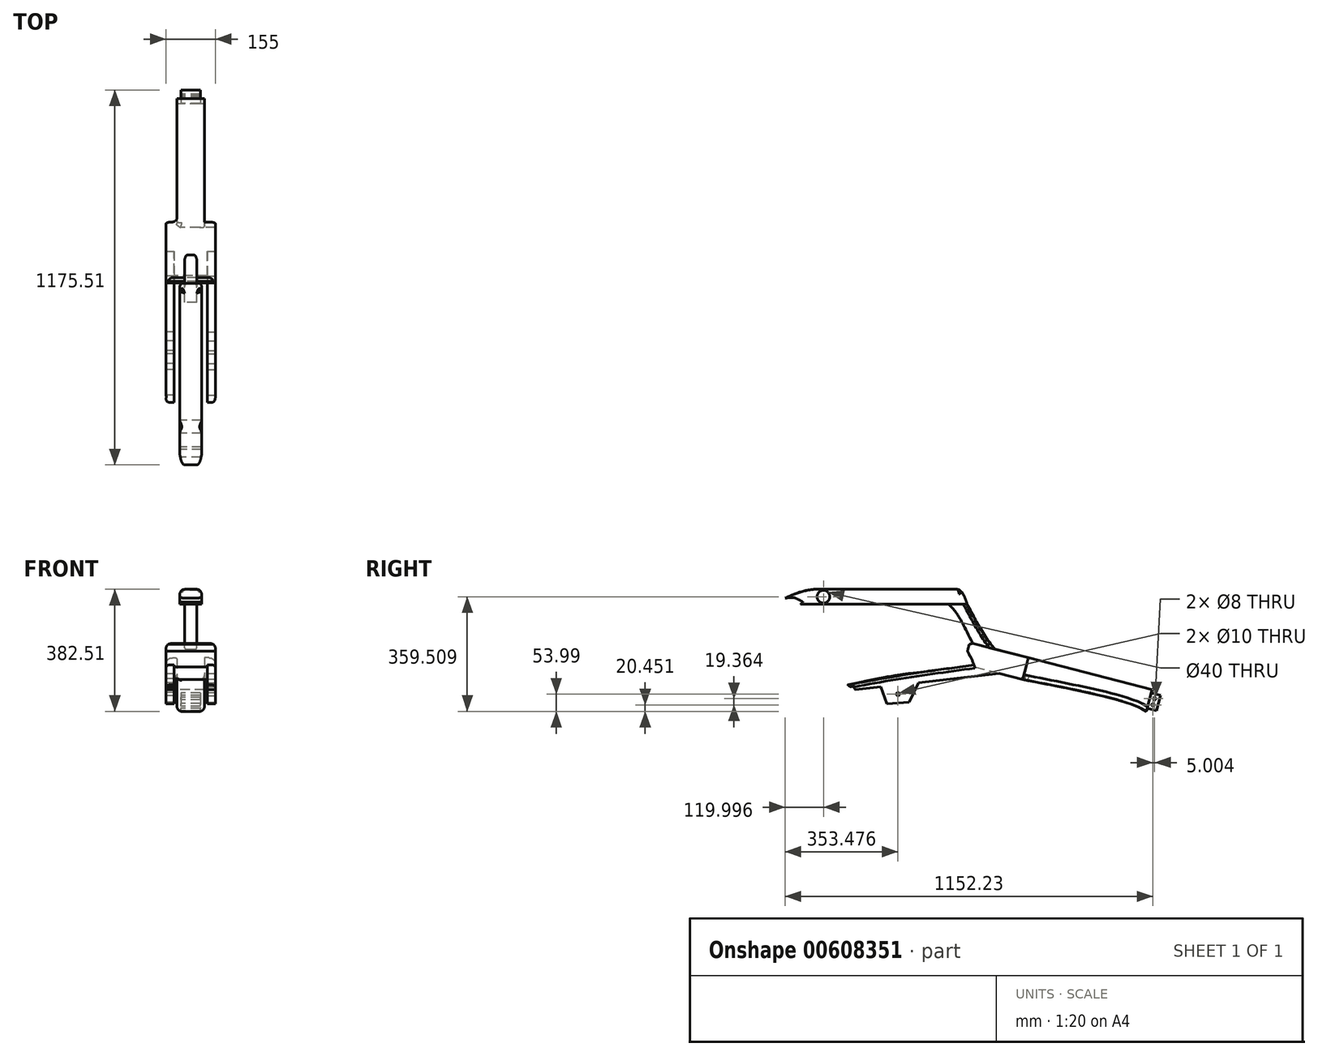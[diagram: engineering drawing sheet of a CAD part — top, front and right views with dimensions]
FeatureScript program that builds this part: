
annotation { "Feature Type Name" : "Feature", "Feature Type Description" : "" }
export const myFeature = defineFeature(function(context is Context, id is Id, definition is map)
    precondition{}
    {
        {
            var Q0;
            Q0=qCreatedBy(makeId("Right.planeOp"),FACE);
            var sketch = newSketch(context, id + "F0", { "sketchPlane" : qUnion([Q0])});
            skLineSegment(sketch, "E0", {"start": v(-839.21, 0) * mm, "end": v(-890, 0) * mm, "construction": true});
            skLineSegment(sketch, "E1", {"start": v(-890, 0) * mm, "end": v(-890, 230) * mm, "construction": true});
            skLineSegment(sketch, "E2", {"start": v(-890, 230) * mm, "end": v(0, 0) * mm, "construction": true});
            skCircle(sketch, "E3", {"center": v(-636.21, 0) * mm, "radius": 203 * mm});
            skCircle(sketch, "E4", {"center": v(513.79, 0) * mm, "radius": 203 * mm});
            skLineSegment(sketch, "E5.bottom", {"start": v(-636.21, 0) * mm, "end": v(513.79, 0) * mm, "construction": true});
            skLineSegment(sketch, "E6", {"start": v(-839.21, 0) * mm, "end": v(-636.21, 0) * mm, "construction": true});
            skCircle(sketch, "E7.0", {"center": v(-636.21, 0) * mm, "radius": 248 * mm});
            skCircle(sketch, "E8.0", {"center": v(513.79, 0) * mm, "radius": 248 * mm});
            skLineSegment(sketch, "E9", {"start": v(0, 0) * mm, "end": v(19.52, 75.52) * mm, "construction": true});
            skLineSegment(sketch, "E10", {"start": v(19.52, 75.52) * mm, "end": v(-870.48, 305.52) * mm, "construction": true});
            skLineSegment(sketch, "E11", {"start": v(-870.48, 305.52) * mm, "end": v(-890, 230) * mm, "construction": true});
            skCircle(sketch, "E12", {"center": v(-870.48, 305.52) * mm, "radius": 22.5 * mm});
            skCircle(sketch, "E13", {"center": v(-870.48, 305.52) * mm, "radius": 21 * mm});
            skCircle(sketch, "E14", {"center": v(-870.48, 305.52) * mm, "radius": 110 * mm});
            skLineSegment(sketch, "E15", {"start": v(19.52, 75.52) * mm, "end": v(573.04, 539.98) * mm, "construction": true});
            skLineSegment(sketch, "E16", {"start": v(-86.27, 75.52) * mm, "end": v(113.73, 75.52) * mm, "construction": true});
            skLineSegment(sketch, "E17", {"start": v(-636.21, 0) * mm, "end": v(-636.21, -248) * mm, "construction": true});
            skLineSegment(sketch, "E18", {"start": v(-636.21, -248) * mm, "end": v(513.79, -248) * mm, "construction": true});
            skLineSegment(sketch, "E19", {"start": v(513.79, -248) * mm, "end": v(513.79, 0) * mm, "construction": true});
            skSolve(sketch);
        }
        {
            var Q0;
            Q0=qCreatedBy(makeId("Right.planeOp"),FACE);
            cPlane(context, id + "F1", {"entities" : qUnion([Q0]), "cplaneType" : CPlaneType.OFFSET, "offset" : 65 * mm, "oppositeDirection" : true, "width" : 150 * mm, "height" : 150 * mm});
        }
        {
            var Q0;
            Q0=qCreatedBy(makeId("Right.planeOp"),FACE);
            cPlane(context, id + "F2", {"entities" : qUnion([Q0]), "cplaneType" : CPlaneType.OFFSET, "offset" : 65 * mm, "width" : 150 * mm, "height" : 150 * mm});
        }
        {
            var Q0;
            Q0=qCreatedBy(makeId("Right.planeOp"),FACE);
            var sketch = newSketch(context, id + "F3", { "sketchPlane" : qUnion([Q0])});
            skLineSegment(sketch, "E20", {"start": v(-228.79, 113.87) * mm, "end": v(158.49, 13.78) * mm});
            skLineSegment(sketch, "E21.bottom", {"start": v(-990.48, 328.52) * mm, "end": v(-420.48, 328.52) * mm, "construction": true});
            skLineSegment(sketch, "E21.top", {"start": v(-990.48, 282.52) * mm, "end": v(-420.48, 282.52) * mm, "construction": true});
            skLineSegment(sketch, "E21.left", {"start": v(-990.48, 328.52) * mm, "end": v(-990.48, 282.52) * mm, "construction": true});
            skLineSegment(sketch, "E21.right", {"start": v(-420.48, 328.52) * mm, "end": v(-420.48, 282.52) * mm, "construction": true});
            skLineSegment(sketch, "E22", {"start": v(-228.79, 113.87) * mm, "end": v(-403.06, 158.9) * mm});
            skLineSegment(sketch, "E23", {"start": v(-412.74, 161.4) * mm, "end": v(-430.26, 93.63) * mm, "construction": true});
            skLineSegment(sketch, "E24", {"start": v(-430.26, 93.63) * mm, "end": v(-246.3, 46.1) * mm, "construction": true});
            skLineSegment(sketch, "E25", {"start": v(158.49, 13.78) * mm, "end": v(140.98, -54) * mm});
            skLineSegment(sketch, "E26", {"start": v(-228.79, 113.87) * mm, "end": v(-246.3, 46.1) * mm});
            skLineSegment(sketch, "E27", {"start": v(-990.48, 305.52) * mm, "end": v(-420.48, 305.52) * mm, "construction": true});
            skLineSegment(sketch, "E28", {"start": v(-420.48, 282.52) * mm, "end": v(-331.58, 140.43) * mm, "construction": true});
            skLineSegment(sketch, "E29", {"start": v(-480.4, 282.52) * mm, "end": v(-403.06, 158.9) * mm, "construction": true});
            skCircle(sketch, "E30", {"center": v(-870.48, 305.52) * mm, "radius": 20 * mm});
            skFitSpline(sketch, "E31", {"points": [v(-446.93, 328.52) * mm, v(-420.48, 282.52) * mm], "startDerivative": vector(40.95, -24.88) * mm, "endDerivative": vector(18.36, -59.68) * mm});
            skLineSegment(sketch, "E32", {"start": v(-480.4, 282.52) * mm, "end": v(-420.48, 282.52) * mm});
            skFitSpline(sketch, "E33", {"points": [v(-480.4, 282.52) * mm, v(-403.06, 158.9) * mm], "startDerivative": vector(83.68, -66.51) * mm, "endDerivative": vector(113.52, -228.08) * mm});
            skFitSpline(sketch, "E34", {"points": [v(-420.48, 282.52) * mm, v(-331.58, 140.43) * mm], "startDerivative": vector(46.18, -95.07) * mm, "endDerivative": vector(81.7, -70.02) * mm});
            skLineSegment(sketch, "E35", {"start": v(-396.57, 84.92) * mm, "end": v(-246.3, 46.1) * mm});
            skFitSpline(sketch, "E36", {"points": [v(-419.66, 134.65) * mm, v(-396.57, 84.92) * mm], "startDerivative": vector(31.98, -52.88) * mm, "endDerivative": vector(7.26, -32.36) * mm});
            skFitSpline(sketch, "E37", {"points": [v(-403.06, 158.9) * mm, v(-414.1, 156.15) * mm], "startDerivative": vector(-13.37, -1.9) * mm, "endDerivative": vector(-11.19, -2.08) * mm});
            skFitSpline(sketch, "E38", {"points": [v(-414.1, 156.15) * mm, v(-419.66, 134.65) * mm], "startDerivative": vector(-4.9, -18.97) * mm, "endDerivative": vector(0.06, 8.38) * mm});
            skLineSegment(sketch, "E39", {"start": v(-430.26, 93.63) * mm, "end": v(140.98, -54) * mm, "construction": true});
            skFitSpline(sketch, "E40", {"points": [v(-246.3, 46.1) * mm, v(140.98, -54) * mm], "startDerivative": vector(593.3, -116.1) * mm, "endDerivative": vector(155.05, -104.97) * mm});
            skCircle(sketch, "E41", {"center": v(166.76, -14.17) * mm, "radius": 4 * mm});
            skCircle(sketch, "E42", {"center": v(161.75, -33.54) * mm, "radius": 4 * mm});
            skLineSegment(sketch, "E43", {"start": v(-900.48, 328.52) * mm, "end": v(-870.48, 305.52) * mm, "construction": true});
            skFitSpline(sketch, "E44", {"points": [v(-900.48, 328.52) * mm, v(-990.48, 301.22) * mm], "startDerivative": vector(-118.47, -11.59) * mm, "endDerivative": vector(-75.39, -34.72) * mm});
            skLineSegment(sketch, "E45", {"start": v(-900.48, 328.52) * mm, "end": v(-446.93, 328.52) * mm});
            skLineSegment(sketch, "E46", {"start": v(-420.48, 282.52) * mm, "end": v(-941.99, 282.52) * mm});
            skFitSpline(sketch, "E47", {"points": [v(-990.48, 301.22) * mm, v(-966.17, 303.05) * mm], "startDerivative": vector(15.61, 2.31) * mm, "endDerivative": vector(15.61, 2.31) * mm});
            skFitSpline(sketch, "E48", {"points": [v(-966.17, 303.05) * mm, v(-934.37, 289.04) * mm], "startDerivative": vector(29.52, -2.6) * mm, "endDerivative": vector(28.82, -13.66) * mm});
            skFitSpline(sketch, "E49", {"points": [v(-934.37, 289.04) * mm, v(-941.99, 282.52) * mm], "startDerivative": vector(-7.1, -7.67) * mm, "endDerivative": vector(-7.31, -5.1) * mm});
            skLineSegment(sketch, "E50", {"start": v(-480.4, 282.52) * mm, "end": v(-361.43, 356.97) * mm, "construction": true});
            skLineSegment(sketch, "E51", {"start": v(-331.58, 140.43) * mm, "end": v(-237.61, 199.22) * mm, "construction": true});
            skLineSegment(sketch, "E52", {"start": v(155.99, 4.1) * mm, "end": v(185.03, -3.4) * mm});
            skLineSegment(sketch, "E53", {"start": v(185.03, -3.4) * mm, "end": v(172.52, -51.81) * mm});
            skLineSegment(sketch, "E54", {"start": v(172.52, -51.81) * mm, "end": v(143.48, -44.3) * mm});
            skLineSegment(sketch, "E55", {"start": v(170.51, 0.35) * mm, "end": v(158, -48.06) * mm, "construction": true});
            skSolve(sketch);
        }
        {
            var Q0;
            Q0=makeQuery(id+"F3.imprint","IMPRINT",FACE,{"disambiguationData":[TD([[makeQuery(id+"F3.imprint","IMPRINT",EDGE,{"derivedFrom":sQuery(id+"F3.wireOp",EDGE,"E30")}),-1.0]])]});
            extrude(context, id + "F4", {"entities" : qUnion([Q0]), "endBound" : BoundingType.SYMMETRIC, "depth" : 68 * mm, "offsetDistance" : 25 * mm});
        }
        {
            var Q0;
            {var subQ0=sQuery(id+"F3.wireOp",EDGE,"E33");Q0=makeQuery(id+"F3.imprint","IMPRINT",FACE,{"disambiguationData":[TD([[makeQuery(id+"F3.imprint","IMPRINT",EDGE,{"derivedFrom":subQ0}),1.0]])]});}
            extrude(context, id + "F5", {"entities" : qUnion([Q0]), "operationType" : NewBodyOperationType.ADD, "endBound" : BoundingType.SYMMETRIC, "depth" : 38.1 * mm, "offsetDistance" : 25 * mm});
        }
        {
            var Q0;
            {var subQ3=sQuery(id+"F3.wireOp",EDGE,"E26");Q0=makeQuery(id+"F3.imprint","IMPRINT",FACE,{"disambiguationData":[TD([[makeQuery(id+"F3.imprint","IMPRINT",EDGE,{"derivedFrom":subQ3}),-1.0]])]});}
            extrude(context, id + "F6", {"entities" : qUnion([Q0]), "operationType" : NewBodyOperationType.ADD, "endBound" : BoundingType.SYMMETRIC, "depth" : 155 * mm, "offsetDistance" : 25 * mm});
        }
        {
            var Q0;
            Q0=makeQuery(id+"F6.opExtrude","CAP_FACE",FACE,{"disambiguationData":[OSD([sQuery(id+"F3.wireOp",EDGE,"E20"),sQuery(id+"F3.wireOp",EDGE,"E22"),sQuery(id+"F3.wireOp",EDGE,"E23"),sQuery(id+"F3.wireOp",EDGE,"E24"),sQuery(id+"F3.wireOp",EDGE,"fels3fzP-0Cul-zycu-sXH3-jASdoxwQIRJ3"),sQuery(id+"F3.wireOp",EDGE,"7BiVgZWP-wgUI-RrVQ-dbGp-AfqpS34TpyPq")])],"isStart":false});
            var sketch = newSketch(context, id + "F7", { "sketchPlane" : qUnion([Q0])});
            skLineSegment(sketch, "E56", {"start": v(-304.09, 102.34) * mm, "end": v(-257.8, 93.53) * mm, "construction": true});
            skLineSegment(sketch, "E57", {"start": v(-257.8, 93.53) * mm, "end": v(-255.41, 72.67) * mm, "construction": true});
            skLineSegment(sketch, "E58", {"start": v(-255.41, 72.67) * mm, "end": v(-791.93, 11.44) * mm, "construction": true});
            skLineSegment(sketch, "E59", {"start": v(-791.93, 11.44) * mm, "end": v(-795.9, 46.22) * mm, "construction": true});
            skLineSegment(sketch, "E60", {"start": v(-795.9, 46.22) * mm, "end": v(-304.09, 102.34) * mm, "construction": true});
            skLineSegment(sketch, "E61", {"start": v(-573.32, 36.39) * mm, "end": v(-601.7, -25.77) * mm});
            skLineSegment(sketch, "E62", {"start": v(-601.7, -25.77) * mm, "end": v(-672.4, -29.77) * mm});
            skLineSegment(sketch, "E63", {"start": v(-672.4, -29.77) * mm, "end": v(-691.03, 22.96) * mm});
            skCircle(sketch, "E64", {"center": v(-637, 0) * mm, "radius": 5 * mm});
            skPoint(sketch, "E65", {"position": v(-320.43, 65.25) * mm});
            skLineSegment(sketch, "E66", {"start": v(-255.41, 72.67) * mm, "end": v(-771.24, 13.8) * mm});
            skFitSpline(sketch, "E67", {"points": [v(-771.24, 13.8) * mm, v(-793.91, 28.83) * mm], "startDerivative": vector(-11.51, 40.5) * mm, "endDerivative": vector(-30.67, 16.33) * mm});
            skLineSegment(sketch, "E68", {"start": v(-304.09, 102.34) * mm, "end": v(-398.53, 91.56) * mm});
            skLineSegment(sketch, "E69", {"start": v(-304.09, 102.34) * mm, "end": v(-257.8, 93.53) * mm});
            skLineSegment(sketch, "E70", {"start": v(-255.41, 72.67) * mm, "end": v(-257.8, 93.53) * mm});
            skFitSpline(sketch, "E71", {"points": [v(-398.53, 91.56) * mm, v(-793.91, 28.83) * mm], "startDerivative": vector(-396.31, -54.62) * mm, "endDerivative": vector(-425.7, -85.53) * mm});
            skSolve(sketch);
        }
        {
            var Q0;
            Q0=makeQuery(id+"F3.imprint","IMPRINT",FACE,{"disambiguationData":[TD([[makeQuery(id+"F3.imprint","IMPRINT",EDGE,{"derivedFrom":sQuery(id+"F3.wireOp",EDGE,"E20")}),-1.0]])]});
            extrude(context, id + "F8", {"entities" : qUnion([Q0]), "operationType" : NewBodyOperationType.ADD, "endBound" : BoundingType.SYMMETRIC, "depth" : 86 * mm, "offsetDistance" : 25 * mm});
        }
        {
            var Q0;
            Q0=makeQuery(id+"F6.opExtrude","CAP_FACE",FACE,{"disambiguationData":[OSD([sQuery(id+"F3.wireOp",EDGE,"E22"),sQuery(id+"F3.wireOp",EDGE,"E23"),sQuery(id+"F3.wireOp",EDGE,"E24"),sQuery(id+"F3.wireOp",EDGE,"E26")])],"isStart":true});
            var sketch = newSketch(context, id + "F9", { "sketchPlane" : qUnion([Q0])});
            skLineSegment(sketch, "E72.0.0", {"start": v(573.32, 36.39) * mm, "end": v(320.43, 65.25) * mm});
            skLineSegment(sketch, "E72.0.1", {"start": v(320.43, 65.25) * mm, "end": v(396.57, 84.92) * mm});
            skFitSpline(sketch, "E72.0.2", {"points": [v(396.57, 84.92) * mm, v(398.98, 95.71) * mm, v(409, 117.02) * mm, v(419.66, 134.65) * mm]});
            skFitSpline(sketch, "E72.0.3", {"points": [v(398.53, 91.56) * mm, v(530.63, 73.36) * mm, v(652.01, 57.34) * mm, v(793.91, 28.83) * mm]});
            skFitSpline(sketch, "E72.0.4", {"points": [v(793.91, 28.83) * mm, v(783.7, 23.39) * mm, v(775.08, 27.3) * mm, v(771.24, 13.8) * mm]});
            skLineSegment(sketch, "E72.0.5", {"start": v(771.24, 13.8) * mm, "end": v(691.03, 22.96) * mm});
            skLineSegment(sketch, "E72.0.6", {"start": v(691.03, 22.96) * mm, "end": v(573.32, 36.39) * mm});
            skLineSegment(sketch, "E73.0.0", {"start": v(601.7, -25.77) * mm, "end": v(573.32, 36.39) * mm});
            skLineSegment(sketch, "E73.0.1", {"start": v(573.32, 36.39) * mm, "end": v(691.03, 22.96) * mm});
            skLineSegment(sketch, "E73.0.2", {"start": v(691.03, 22.96) * mm, "end": v(672.4, -29.77) * mm});
            skLineSegment(sketch, "E73.0.3", {"start": v(672.4, -29.77) * mm, "end": v(601.7, -25.77) * mm});
            skCircle(sketch, "E74.0", {"center": v(637, 0) * mm, "radius": 5 * mm});
            skLineSegment(sketch, "E75.0.0", {"start": v(257.8, 93.53) * mm, "end": v(304.09, 102.34) * mm});
            skLineSegment(sketch, "E75.0.1", {"start": v(304.09, 102.34) * mm, "end": v(398.53, 91.56) * mm});
            skFitSpline(sketch, "E75.0.2", {"points": [v(419.66, 134.65) * mm, v(409, 117.02) * mm, v(398.98, 95.71) * mm, v(396.57, 84.92) * mm]});
            skLineSegment(sketch, "E75.0.3", {"start": v(396.57, 84.92) * mm, "end": v(320.43, 65.25) * mm});
            skLineSegment(sketch, "E75.0.4", {"start": v(320.43, 65.25) * mm, "end": v(255.41, 72.67) * mm});
            skLineSegment(sketch, "E75.0.5", {"start": v(255.41, 72.67) * mm, "end": v(257.8, 93.53) * mm});
            skSolve(sketch);
        }
        {
            var Q0;
            Q0=makeQuery(id+"F3.imprint","IMPRINT",FACE,{"disambiguationData":[TD([[makeQuery(id+"F3.imprint","IMPRINT",EDGE,{"derivedFrom":sQuery(id+"F3.wireOp",EDGE,"E41")}),-1.0]])]});
            extrude(context, id + "F10", {"entities" : qUnion([Q0]), "operationType" : NewBodyOperationType.ADD, "endBound" : BoundingType.SYMMETRIC, "depth" : 60 * mm, "offsetDistance" : 25 * mm});
        }
        {
            var Q0;
            {var subQ0=sQuery(id+"F7.wireOp",EDGE,"E67");Q0=makeQuery(id+"F7.imprint","IMPRINT",FACE,{"disambiguationData":[TD([[makeQuery(id+"F7.imprint","IMPRINT",EDGE,{"derivedFrom":subQ0}),-1.0]])]});}
            var Q1;
            {var subQ1=sQuery(id+"F7.wireOp",EDGE,"E61");Q1=makeQuery(id+"F7.imprint","IMPRINT",FACE,{"disambiguationData":[TD([[makeQuery(id+"F7.imprint","IMPRINT",EDGE,{"derivedFrom":subQ1}),-1.0]])]});}
            var Q2;
            {var subQ1=sQuery(id+"F7.wireOp",EDGE,"E68");Q2=makeQuery(id+"F7.imprint","IMPRINT",FACE,{"disambiguationData":[TD([[makeQuery(id+"F7.imprint","IMPRINT",EDGE,{"derivedFrom":subQ1}),1.0]])]});}
            extrude(context, id + "F11", {"entities" : qUnion([Q0, Q1, Q2]), "operationType" : NewBodyOperationType.ADD, "oppositeDirection" : true, "depth" : 25.4 * mm, "offsetDistance" : 25 * mm});
        }
        {
            var Q0;
            Q0=makeQuery(id+"F8.opExtrude","CAP_EDGE",EDGE,{"disambiguationData":[OSD([sQuery(id+"F3.wireOp",EDGE,"E26")])],"isStart":true});
            var Q1;
            Q1=makeQuery(id+"F8.opExtrude","CAP_EDGE",EDGE,{"disambiguationData":[OSD([sQuery(id+"F3.wireOp",EDGE,"E26")])],"isStart":false});
            var Q2;
            Q2=makeQuery(id+"F4.opExtrude","CAP_EDGE",EDGE,{"disambiguationData":[OSD([sQuery(id+"F3.wireOp",EDGE,"E45")])],"isStart":false});
            var Q3;
            Q3=makeQuery(id+"F4.opExtrude","CAP_EDGE",EDGE,{"disambiguationData":[OSD([sQuery(id+"F3.wireOp",EDGE,"E45")])],"isStart":true});
            var Q4;
            Q4=makeQuery(id+"F4.opExtrude","CAP_EDGE",EDGE,{"disambiguationData":[OSD([sQuery(id+"F3.wireOp",EDGE,"E44")])],"isStart":false});
            var Q5;
            Q5=makeQuery(id+"F4.opExtrude","CAP_EDGE",EDGE,{"disambiguationData":[OSD([sQuery(id+"F3.wireOp",EDGE,"E44")])],"isStart":true});
            var Q6;
            Q6=makeQuery(id+"F4.opExtrude","SWEPT_EDGE",EDGE,{"disambiguationData":[OSD([sQuery(id+"F3.wireOp",EDGE,"E31"),sQuery(id+"F3.wireOp",EDGE,"E45")])]});
            var Q7;
            Q7=makeQuery(id+"F4.opExtrude","SWEPT_EDGE",EDGE,{"disambiguationData":[OSD([sQuery(id+"F3.wireOp",EDGE,"E44"),sQuery(id+"F3.wireOp",EDGE,"E45")])]});
            fillet(context, id + "F12", {"entities" : qUnion([Q0, Q1, Q2, Q3, Q4, Q5, Q6, Q7]), "radius" : 15 * mm, "tangentPropagation" : true, "allowEdgeOverflow" : false});
        }
        {
            var Q0;
            Q0=makeQuery(id+"F5.opExtrude","CAP_EDGE",EDGE,{"disambiguationData":[OSD([sQuery(id+"F3.wireOp",EDGE,"E34")])],"isStart":false});
            var Q1;
            Q1=makeQuery(id+"F5.opExtrude","CAP_EDGE",EDGE,{"disambiguationData":[OSD([sQuery(id+"F3.wireOp",EDGE,"E34")])],"isStart":true});
            var Q2;
            Q2=makeQuery(id+"F11.opExtrude","CAP_EDGE",EDGE,{"disambiguationData":[OSD([sQuery(id+"F7.wireOp",EDGE,"2d2ba40c-a02e-4269-819a-9c400366be13")])],"isStart":true});
            var Q3;
            Q3=makeQuery(id+"FFKQbZDGYRM2YjH_1.opExtrude","CAP_EDGE",EDGE,{"disambiguationData":[OSD([sQuery(id+"F9.wireOp",EDGE,"418496da-3a12-4d16-a20d-26360628b4ec.2")])],"isStart":true});
            var Q4;
            Q4=makeQuery(id+"F4.opExtrude","CAP_EDGE",EDGE,{"disambiguationData":[OSD([sQuery(id+"F3.wireOp",EDGE,"E31")])],"isStart":false});
            var Q5;
            Q5=makeQuery(id+"F4.opExtrude","CAP_EDGE",EDGE,{"disambiguationData":[OSD([sQuery(id+"F3.wireOp",EDGE,"E31")])],"isStart":true});
            fillet(context, id + "F13", {"entities" : qUnion([Q0, Q1, Q2, Q3, Q4, Q5]), "radius" : 10 * mm, "tangentPropagation" : true, "allowEdgeOverflow" : false});
        }
        {
            var Q0;
            Q0=makeQuery(id+"F4.opExtrude","CAP_EDGE",EDGE,{"disambiguationData":[OSD([sQuery(id+"F3.wireOp",EDGE,"81e0ebba-2043-46d8-adfa-aa85b01486f9")])],"isStart":true});
            var Q1;
            Q1=makeQuery(id+"F4.opExtrude","CAP_EDGE",EDGE,{"disambiguationData":[OSD([sQuery(id+"F3.wireOp",EDGE,"81e0ebba-2043-46d8-adfa-aa85b01486f9")])],"isStart":false});
            var Q2;
            Q2=makeQuery(id+"F6.opExtrude","CAP_EDGE",EDGE,{"disambiguationData":[OSD([sQuery(id+"F3.wireOp",EDGE,"E22")])],"isStart":false});
            var Q3;
            Q3=makeQuery(id+"F6.opExtrude","CAP_EDGE",EDGE,{"disambiguationData":[OSD([sQuery(id+"F3.wireOp",EDGE,"E22")])],"isStart":true});
            fillet(context, id + "F14", {"entities" : qUnion([Q0, Q1, Q2, Q3]), "radius" : 20 * mm, "tangentPropagation" : true, "allowEdgeOverflow" : false});
        }
        {
            var Q0;
            Q0=makeQuery(id+"F8.opExtrude","CAP_EDGE",EDGE,{"disambiguationData":[OSD([sQuery(id+"F3.wireOp",EDGE,"E40")])],"isStart":false});
            var Q1;
            Q1=makeQuery(id+"F8.opExtrude","CAP_EDGE",EDGE,{"disambiguationData":[OSD([sQuery(id+"F3.wireOp",EDGE,"E40")])],"isStart":true});
            fillet(context, id + "F15", {"entities" : qUnion([Q0, Q1]), "radius" : 15 * mm, "tangentPropagation" : true, "allowEdgeOverflow" : false});
        }
        {
            var Q0;
            Q0=makeQuery(id+"F9.imprint","IMPRINT",FACE,{"disambiguationData":[TD([[makeQuery(id+"F9.imprint","IMPRINT",EDGE,{"derivedFrom":sQuery(id+"F9.wireOp",EDGE,"E72.0.0")}),-1.0]])]});
            var Q1;
            Q1=makeQuery(id+"F9.imprint","IMPRINT",FACE,{"disambiguationData":[TD([[makeQuery(id+"F9.imprint","IMPRINT",EDGE,{"derivedFrom":sQuery(id+"F9.wireOp",EDGE,"E75.0.0")}),-1.0]])]});
            var Q2;
            Q2=makeQuery(id+"F9.imprint","IMPRINT",FACE,{"disambiguationData":[TD([[makeQuery(id+"F9.imprint","IMPRINT",EDGE,{"derivedFrom":sQuery(id+"F9.wireOp",EDGE,"E73.0.0")}),-1.0]])]});
            extrude(context, id + "F16", {"entities" : qUnion([Q0, Q1, Q2]), "operationType" : NewBodyOperationType.ADD, "oppositeDirection" : true, "depth" : 25 * mm, "offsetDistance" : 25 * mm});
        }
        {
            var Q0;
            Q0=makeQuery(id+"F16.opExtrude","CAP_EDGE",EDGE,{"disambiguationData":[OSD([sQuery(id+"F9.wireOp",EDGE,"E72.0.3")])],"isStart":true});
            var Q1;
            Q1=makeQuery(id+"F11.opExtrude","CAP_EDGE",EDGE,{"disambiguationData":[OSD([sQuery(id+"F7.wireOp",EDGE,"E71")])],"isStart":true});
            fillet(context, id + "F17", {"entities" : qUnion([Q0, Q1]), "radius" : 10 * mm, "tangentPropagation" : true, "allowEdgeOverflow" : false});
        }
    });
